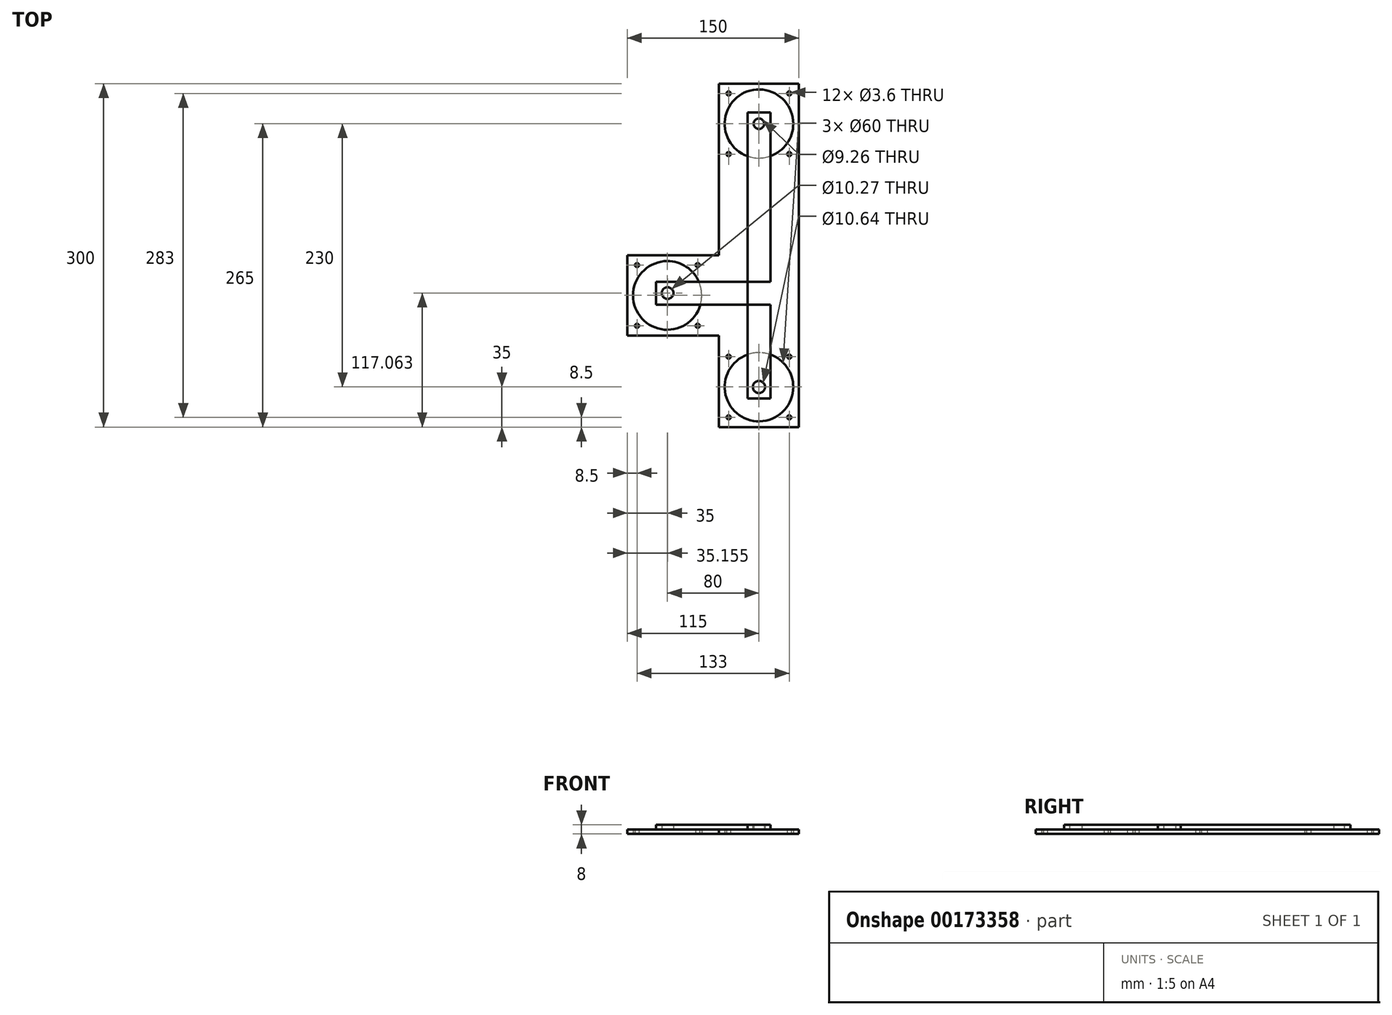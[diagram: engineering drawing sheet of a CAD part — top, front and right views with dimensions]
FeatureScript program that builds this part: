
annotation { "Feature Type Name" : "Feature", "Feature Type Description" : "" }
export const myFeature = defineFeature(function(context is Context, id is Id, definition is map)
    precondition{}
    {
        {
            var Q0;
            Q0=qCreatedBy(makeId("Top.planeOp"),FACE);
            var sketch = newSketch(context, id + "F0", { "sketchPlane" : qUnion([Q0])});
            skLineSegment(sketch, "E0.bottom", {"start": v(-35, 150) * mm, "end": v(35, 150) * mm});
            skLineSegment(sketch, "E0.left", {"start": v(-35, 150) * mm, "end": v(-35, 0) * mm});
            skLineSegment(sketch, "E0.right", {"start": v(35, 150) * mm, "end": v(35, 0) * mm});
            skLineSegment(sketch, "E1.bottom", {"start": v(-26.5, 141.5) * mm, "end": v(26.5, 141.5) * mm, "construction": true});
            skLineSegment(sketch, "E1.top", {"start": v(-26.5, 88.5) * mm, "end": v(26.5, 88.5) * mm, "construction": true});
            skLineSegment(sketch, "E1.left", {"start": v(-26.5, 141.5) * mm, "end": v(-26.5, 88.5) * mm, "construction": true});
            skLineSegment(sketch, "E1.right", {"start": v(26.5, 141.5) * mm, "end": v(26.5, 88.5) * mm, "construction": true});
            skPoint(sketch, "E2", {"position": v(0, 141.5) * mm});
            skPoint(sketch, "E3", {"position": v(-26.5, 115) * mm});
            skPoint(sketch, "E4", {"position": v(0, 150) * mm});
            skCircle(sketch, "E5", {"center": v(-26.5, 141.5) * mm, "radius": 1.8 * mm});
            skCircle(sketch, "E6", {"center": v(-26.5, 88.5) * mm, "radius": 1.8 * mm});
            skCircle(sketch, "E7", {"center": v(26.5, 141.5) * mm, "radius": 1.8 * mm});
            skCircle(sketch, "E8", {"center": v(26.5, 88.5) * mm, "radius": 1.8 * mm});
            skCircle(sketch, "E9", {"center": v(0, 115) * mm, "radius": 30 * mm});
            skLineSegment(sketch, "E10", {"start": v(35, 0) * mm, "end": v(134.17, -99.17) * mm});
            skLineSegment(sketch, "E11", {"start": v(35, 0) * mm, "end": v(-35, 0) * mm});
            skSolve(sketch);
        }
        {
            var Q0;
            Q0=makeQuery(id+"F0.imprint","IMPRINT",FACE,{"disambiguationData":[TD([[makeQuery(id+"F0.imprint","IMPRINT",EDGE,{"derivedFrom":sQuery(id+"F0.wireOp",EDGE,"E0.bottom")}),-1.0]])]});
            extrude(context, id + "F1", {"entities" : qUnion([Q0]), "depth" : 4 * mm});
        }
        {
            var Q0;
            Q0=makeQuery(id+"F1.opExtrude","SWEPT_BODY",BODY,{"disambiguationData":[OSD([sQuery(id+"F0.wireOp",EDGE,"E0.bottom"),sQuery(id+"F0.wireOp",EDGE,"E0.left"),sQuery(id+"F0.wireOp",EDGE,"E0.right"),sQuery(id+"F0.wireOp",EDGE,"E5"),sQuery(id+"F0.wireOp",EDGE,"E6"),sQuery(id+"F0.wireOp",EDGE,"E7"),sQuery(id+"F0.wireOp",EDGE,"E8"),sQuery(id+"F0.wireOp",EDGE,"E9"),sQuery(id+"F0.wireOp",EDGE,"E11")])]});
            var Q1;
            Q1=qCreatedBy(makeId("Front.planeOp"),FACE);
            mirror(context, id + "F2", {"entities" : qUnion([Q0]), "mirrorPlane" : qUnion([Q1])});
        }
        {
            var Q0;
            Q0=makeQuery(id+"F1.opExtrude","SWEPT_BODY",BODY,{"disambiguationData":[OSD([sQuery(id+"F0.wireOp",EDGE,"E0.bottom"),sQuery(id+"F0.wireOp",EDGE,"E0.left"),sQuery(id+"F0.wireOp",EDGE,"E0.right"),sQuery(id+"F0.wireOp",EDGE,"E5"),sQuery(id+"F0.wireOp",EDGE,"E6"),sQuery(id+"F0.wireOp",EDGE,"E7"),sQuery(id+"F0.wireOp",EDGE,"E8"),sQuery(id+"F0.wireOp",EDGE,"E9"),sQuery(id+"F0.wireOp",EDGE,"E11")])]});
            var Q1;
            Q1=makeQuery(id+"F2.opPattern","COPY",EDGE,{"derivedFrom":makeQuery(id+"F1.opExtrude","SWEPT_EDGE",EDGE,{"disambiguationData":[OSD([sQuery(id+"F0.wireOp",EDGE,"E0.right"),sQuery(id+"F0.wireOp",EDGE,"E11")])]}),"instanceName":"1"});
            transform(context, id + "F3", {"entities" : qUnion([Q0]), "transformType" : TransformType.ROTATION, "transformAxis" : qUnion([Q1]), "angle" : 270 * degree, "makeCopy" : true});
        }
        {
            var Q0;
            Q0=makeQuery(id+"F1.opExtrude","SWEPT_BODY",BODY,{"disambiguationData":[OSD([sQuery(id+"F0.wireOp",EDGE,"E0.bottom"),sQuery(id+"F0.wireOp",EDGE,"E0.left"),sQuery(id+"F0.wireOp",EDGE,"E0.right"),sQuery(id+"F0.wireOp",EDGE,"E5"),sQuery(id+"F0.wireOp",EDGE,"E6"),sQuery(id+"F0.wireOp",EDGE,"E7"),sQuery(id+"F0.wireOp",EDGE,"E8"),sQuery(id+"F0.wireOp",EDGE,"E9"),sQuery(id+"F0.wireOp",EDGE,"E11")])]});
            var Q1;
            Q1=makeQuery(id+"F3.opPattern","COPY",BODY,{"derivedFrom":makeQuery(id+"F1.opExtrude","SWEPT_BODY",BODY,{"disambiguationData":[OSD([sQuery(id+"F0.wireOp",EDGE,"E0.bottom"),sQuery(id+"F0.wireOp",EDGE,"E0.left"),sQuery(id+"F0.wireOp",EDGE,"E0.right"),sQuery(id+"F0.wireOp",EDGE,"E5"),sQuery(id+"F0.wireOp",EDGE,"E6"),sQuery(id+"F0.wireOp",EDGE,"E7"),sQuery(id+"F0.wireOp",EDGE,"E8"),sQuery(id+"F0.wireOp",EDGE,"E9"),sQuery(id+"F0.wireOp",EDGE,"E11")])]}),"instanceName":"1"});
            var Q2;
            Q2=makeQuery(id+"F2.opPattern","COPY",BODY,{"derivedFrom":makeQuery(id+"F1.opExtrude","SWEPT_BODY",BODY,{"disambiguationData":[OSD([sQuery(id+"F0.wireOp",EDGE,"E0.bottom"),sQuery(id+"F0.wireOp",EDGE,"E0.left"),sQuery(id+"F0.wireOp",EDGE,"E0.right"),sQuery(id+"F0.wireOp",EDGE,"E5"),sQuery(id+"F0.wireOp",EDGE,"E6"),sQuery(id+"F0.wireOp",EDGE,"E7"),sQuery(id+"F0.wireOp",EDGE,"E8"),sQuery(id+"F0.wireOp",EDGE,"E9"),sQuery(id+"F0.wireOp",EDGE,"E11")])]}),"instanceName":"1"});
            booleanBodies(context, id + "F4", {"operationType" : BooleanOperationType.UNION, "tools" : qUnion([Q0, Q1, Q2])});
        }
        {
            var Q0;
            {var subQ0=makeQuery(id+"F1.opExtrude","CAP_FACE",FACE,{"disambiguationData":[OSD([sQuery(id+"F0.wireOp",EDGE,"E0.bottom"),sQuery(id+"F0.wireOp",EDGE,"E0.left"),sQuery(id+"F0.wireOp",EDGE,"E0.right"),sQuery(id+"F0.wireOp",EDGE,"E5"),sQuery(id+"F0.wireOp",EDGE,"E6"),sQuery(id+"F0.wireOp",EDGE,"E7"),sQuery(id+"F0.wireOp",EDGE,"E8"),sQuery(id+"F0.wireOp",EDGE,"E9"),sQuery(id+"F0.wireOp",EDGE,"E11")])],"isStart":false});Q0=makeQuery(id+"F4.opBoolean","MERGE",FACE,{"derivedFrom":[subQ0,makeQuery(id+"F2.opPattern","COPY",FACE,{"derivedFrom":subQ0,"instanceName":"1"}),makeQuery(id+"F3.opPattern","COPY",FACE,{"derivedFrom":subQ0,"instanceName":"1"})]});}
            var sketch = newSketch(context, id + "F5", { "sketchPlane" : qUnion([Q0])});
            skLineSegment(sketch, "E12.bottom", {"start": v(-10, 125) * mm, "end": v(10, 125) * mm});
            skLineSegment(sketch, "E12.top", {"start": v(-10, -125) * mm, "end": v(10, -125) * mm});
            skLineSegment(sketch, "E12.left", {"start": v(-10, 125) * mm, "end": v(-10, -125) * mm});
            skLineSegment(sketch, "E12.right", {"start": v(10, 125) * mm, "end": v(10, -125) * mm});
            skLineSegment(sketch, "E13.bottom", {"start": v(-89.84, -23.17) * mm, "end": v(10, -23.17) * mm});
            skLineSegment(sketch, "E13.top", {"start": v(-89.84, -43.17) * mm, "end": v(10, -43.17) * mm});
            skLineSegment(sketch, "E13.left", {"start": v(-89.84, -23.17) * mm, "end": v(-89.84, -43.17) * mm});
            skLineSegment(sketch, "E13.right", {"start": v(10, -23.17) * mm, "end": v(10, -43.17) * mm});
            skCircle(sketch, "E14", {"center": v(0, 115) * mm, "radius": 4.63 * mm});
            skCircle(sketch, "E15", {"center": v(-79.84, -32.94) * mm, "radius": 5.14 * mm});
            skCircle(sketch, "E16", {"center": v(0, -115) * mm, "radius": 5.32 * mm});
            skCircle(sketch, "E17", {"center": v(0, -33.17) * mm, "radius": 6 * mm});
            skSolve(sketch);
        }
        {
            var Q0;
            {var subQ5=sQuery(id+"F5.wireOp",EDGE,"E13.right");Q0=makeQuery(id+"F5.imprint","IMPRINT",FACE,{"disambiguationData":[TD([[makeQuery(id+"F5.imprint","IMPRINT",EDGE,{"derivedFrom":subQ5}),-1.0]])]});}
            var Q1;
            {var subQ0=sQuery(id+"F5.wireOp",EDGE,"E13.top");var subQ1=sQuery(id+"F5.wireOp",EDGE,"E12.left");var subQ2=makeQuery(id+"F5.imprint","INTERSECT",VERTEX,{"derivedFrom":[subQ1,subQ0]});Q1=makeQuery(id+"F5.imprint","IMPRINT",FACE,{"disambiguationData":[TD([[makeQuery(id+"F5.imprint","IMPRINT",EDGE,{"disambiguationData":[TD([[subQ2,-1.0]])],"derivedFrom":subQ1}),1.0]])]});}
            var Q2;
            {var subQ5=sQuery(id+"F5.wireOp",EDGE,"E12.top");Q2=makeQuery(id+"F5.imprint","IMPRINT",FACE,{"disambiguationData":[TD([[makeQuery(id+"F5.imprint","IMPRINT",EDGE,{"derivedFrom":subQ5}),1.0]])]});}
            var Q3;
            {var subQ0=sQuery(id+"F5.wireOp",EDGE,"E13.bottom");var subQ1=sQuery(id+"F5.wireOp",EDGE,"E12.left");var subQ2=makeQuery(id+"F5.imprint","INTERSECT",VERTEX,{"derivedFrom":[subQ1,subQ0]});Q3=makeQuery(id+"F5.imprint","IMPRINT",FACE,{"disambiguationData":[TD([[makeQuery(id+"F5.imprint","IMPRINT",EDGE,{"disambiguationData":[TD([[subQ2,-1.0]])],"derivedFrom":subQ1}),-1.0]])]});}
            var Q4;
            {var subQ0=sQuery(id+"F5.wireOp",EDGE,"E13.left");Q4=makeQuery(id+"F5.imprint","IMPRINT",FACE,{"disambiguationData":[TD([[makeQuery(id+"F5.imprint","IMPRINT",EDGE,{"derivedFrom":subQ0}),1.0]])]});}
            var Q5;
            {var subQ0=sQuery(id+"F5.wireOp",EDGE,"E13.bottom");var subQ1=sQuery(id+"F5.wireOp",EDGE,"E12.left");var subQ2=makeQuery(id+"F5.imprint","INTERSECT",VERTEX,{"derivedFrom":[subQ1,subQ0]});Q5=makeQuery(id+"F5.imprint","IMPRINT",FACE,{"disambiguationData":[TD([[makeQuery(id+"F5.imprint","IMPRINT",EDGE,{"disambiguationData":[TD([[subQ2,1.0]])],"derivedFrom":subQ1}),1.0]])]});}
            var Q6;
            {var subQ5=sQuery(id+"F5.wireOp",EDGE,"E12.bottom");Q6=makeQuery(id+"F5.imprint","IMPRINT",FACE,{"disambiguationData":[TD([[makeQuery(id+"F5.imprint","IMPRINT",EDGE,{"derivedFrom":subQ5}),-1.0]])]});}
            extrude(context, id + "F6", {"entities" : qUnion([Q0, Q1, Q2, Q3, Q4, Q5, Q6]), "depth" : 4 * mm});
        }
    });
